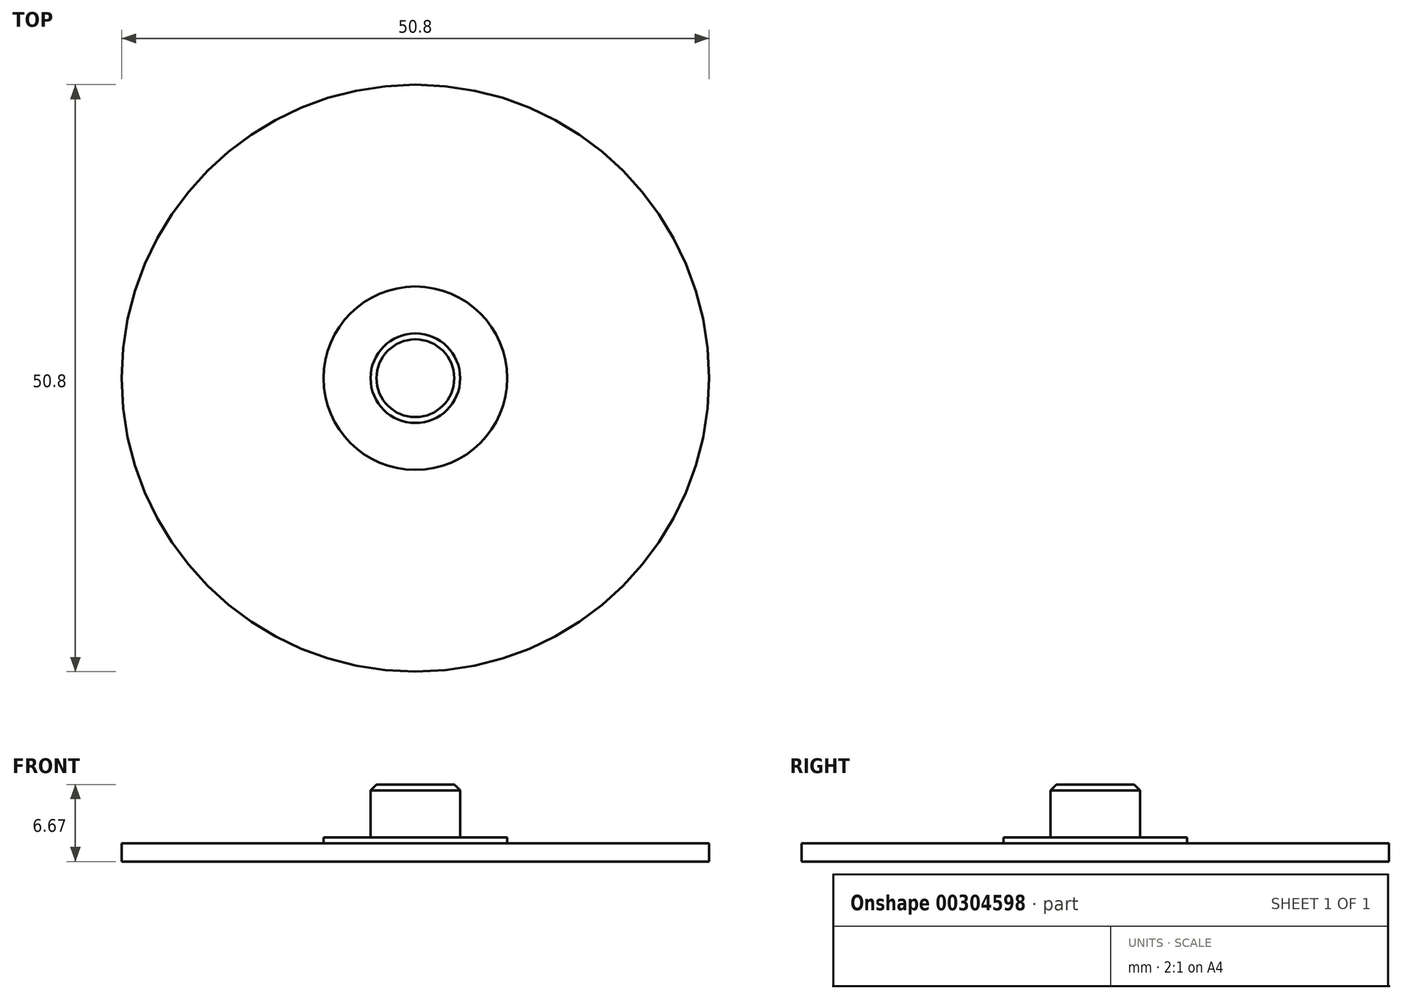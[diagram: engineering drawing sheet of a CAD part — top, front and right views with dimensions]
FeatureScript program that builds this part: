
annotation { "Feature Type Name" : "Feature", "Feature Type Description" : "" }
export const myFeature = defineFeature(function(context is Context, id is Id, definition is map)
    precondition{}
    {
        {
            var Q0;
            Q0=qCreatedBy(makeId("Top.planeOp"),FACE);
            var sketch = newSketch(context, id + "F0", { "sketchPlane" : qUnion([Q0])});
            skCircle(sketch, "E0", {"center": v(0, 0) * mm, "radius": 25.4 * mm});
            skCircle(sketch, "E1", {"center": v(0, 0) * mm, "radius": 3.87 * mm});
            skCircle(sketch, "E2", {"center": v(0, 0) * mm, "radius": 7.94 * mm});
            skSolve(sketch);
        }
        {
            var Q0;
            Q0=makeQuery(id+"F0.imprint","IMPRINT",FACE,{"disambiguationData":[TD([[makeQuery(id+"F0.imprint","IMPRINT",EDGE,{"derivedFrom":sQuery(id+"F0.wireOp",EDGE,"E0")}),1.0]])]});
            var Q1;
            Q1=makeQuery(id+"F0.imprint","IMPRINT",FACE,{"disambiguationData":[TD([[makeQuery(id+"F0.imprint","IMPRINT",EDGE,{"derivedFrom":sQuery(id+"F0.wireOp",EDGE,"E1")}),1.0]])]});
            var Q2;
            Q2=makeQuery(id+"F0.imprint","IMPRINT",FACE,{"disambiguationData":[TD([[makeQuery(id+"F0.imprint","IMPRINT",EDGE,{"derivedFrom":sQuery(id+"F0.wireOp",EDGE,"E1")}),-1.0]])]});
            extrude(context, id + "F1", {"entities" : qUnion([Q0, Q1, Q2]), "oppositeDirection" : true, "depth" : 1.59 * mm});
        }
        {
            var Q0;
            Q0=makeQuery(id+"F0.imprint","IMPRINT",FACE,{"disambiguationData":[TD([[makeQuery(id+"F0.imprint","IMPRINT",EDGE,{"derivedFrom":sQuery(id+"F0.wireOp",EDGE,"E1")}),1.0]])]});
            extrude(context, id + "F2", {"entities" : qUnion([Q0]), "operationType" : NewBodyOperationType.ADD, "offsetDistance" : 25.4 * mm, "depth" : 5.08 * mm});
        }
        {
            var Q0;
            Q0=makeQuery(id+"F2.opExtrude","CAP_EDGE",EDGE,{"disambiguationData":[OSD([sQuery(id+"F0.wireOp",EDGE,"E1")])],"isStart":false});
            chamfer(context, id + "F3", {"entities" : qUnion([Q0]), "width" : 0.5 * mm, "tangentPropagation" : true});
        }
        {
            var Q0;
            Q0=makeQuery(id+"F0.imprint","IMPRINT",FACE,{"disambiguationData":[TD([[makeQuery(id+"F0.imprint","IMPRINT",EDGE,{"derivedFrom":sQuery(id+"F0.wireOp",EDGE,"E1")}),-1.0]])]});
            extrude(context, id + "F4", {"entities" : qUnion([Q0]), "operationType" : NewBodyOperationType.ADD, "offsetDistance" : 25.4 * mm, "depth" : 0.5 * mm});
        }
    });
